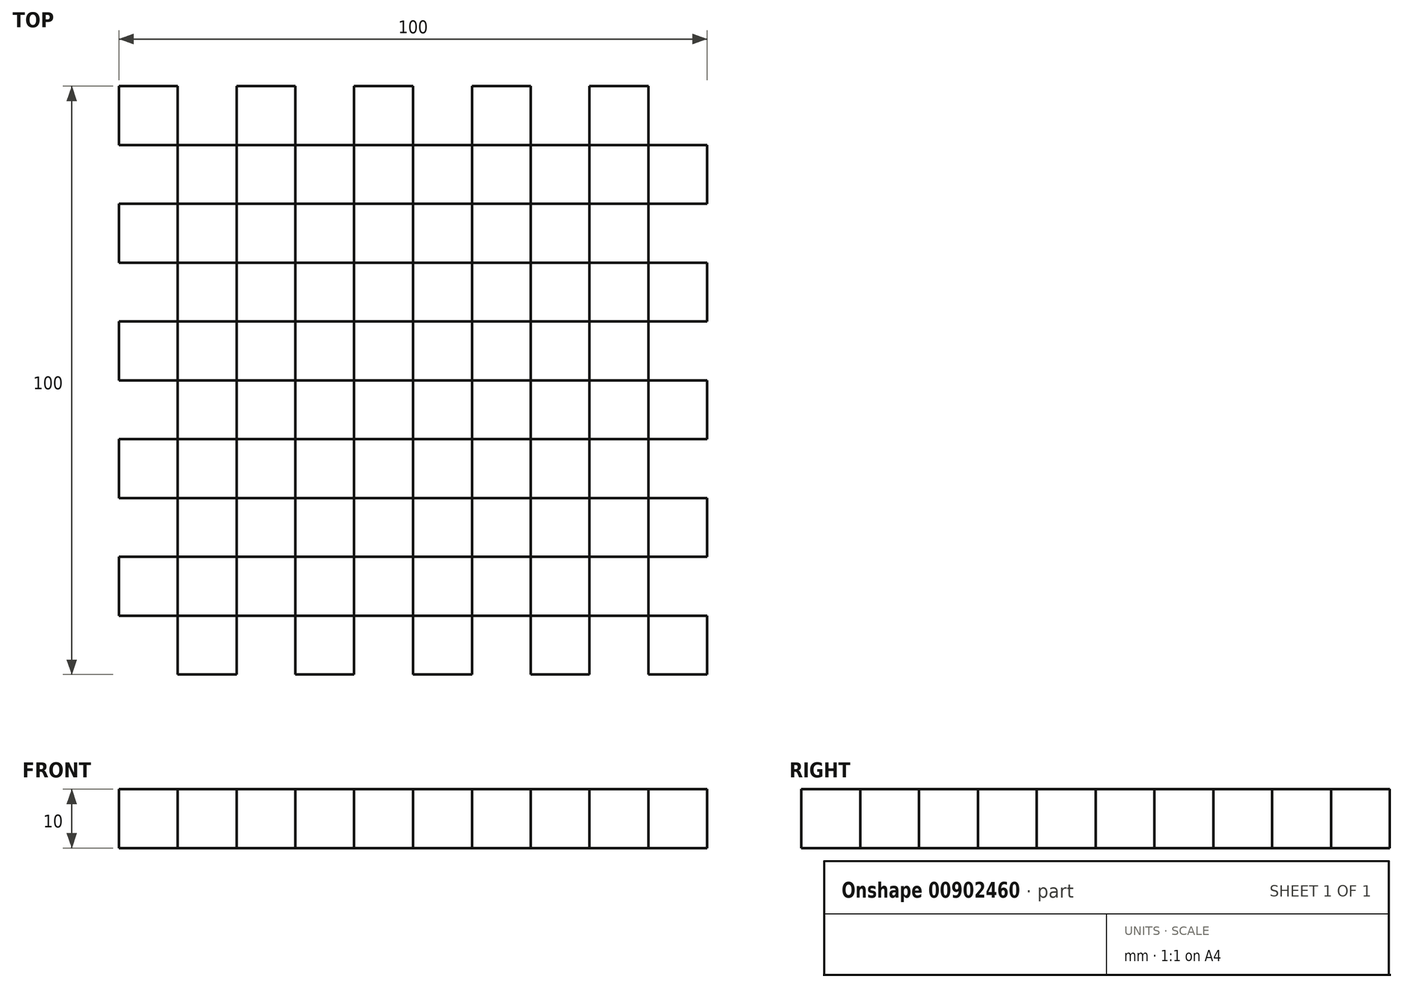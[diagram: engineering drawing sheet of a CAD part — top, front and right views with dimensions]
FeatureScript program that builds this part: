
annotation { "Feature Type Name" : "Feature", "Feature Type Description" : "" }
export const myFeature = defineFeature(function(context is Context, id is Id, definition is map)
    precondition{}
    {
        {
            var Q0;
            Q0=qCreatedBy(makeId("Top.planeOp"),FACE);
            var sketch = newSketch(context, id + "F0", { "sketchPlane" : qUnion([Q0])});
            skLineSegment(sketch, "E0.bottom", {"start": v(-50, 50) * mm, "end": v(50, 50) * mm});
            skLineSegment(sketch, "E0.top", {"start": v(-50, -50) * mm, "end": v(50, -50) * mm});
            skLineSegment(sketch, "E0.left", {"start": v(-50, 50) * mm, "end": v(-50, -50) * mm});
            skLineSegment(sketch, "E0.right", {"start": v(50, 50) * mm, "end": v(50, -50) * mm});
            skLineSegment(sketch, "E1", {"start": v(0, 0) * mm, "end": v(0, 50) * mm, "construction": true});
            skLineSegment(sketch, "E2", {"start": v(0, 0) * mm, "end": v(-50, 0) * mm, "construction": true});
            skLineSegment(sketch, "E3", {"start": v(-50, 40) * mm, "end": v(50, 40) * mm});
            skLineSegment(sketch, "E4", {"start": v(-50, 30) * mm, "end": v(50, 30) * mm});
            skLineSegment(sketch, "E5", {"start": v(-50, 20) * mm, "end": v(50, 20) * mm});
            skLineSegment(sketch, "E6", {"start": v(-50, 10) * mm, "end": v(50, 10) * mm});
            skLineSegment(sketch, "E7", {"start": v(-50, 0) * mm, "end": v(50, 0) * mm});
            skLineSegment(sketch, "E8.MirrorCS", {"start": v(-50, -40) * mm, "end": v(50, -40) * mm});
            skLineSegment(sketch, "E9.MirrorCS", {"start": v(-50, -30) * mm, "end": v(50, -30) * mm});
            skLineSegment(sketch, "E10.MirrorCS", {"start": v(-50, -20) * mm, "end": v(50, -20) * mm});
            skLineSegment(sketch, "E11.MirrorCS", {"start": v(-50, -10) * mm, "end": v(50, -10) * mm});
            skLineSegment(sketch, "E12", {"start": v(-40, 50) * mm, "end": v(-40, -50) * mm});
            skLineSegment(sketch, "E13", {"start": v(-30, 50) * mm, "end": v(-30, -50) * mm});
            skLineSegment(sketch, "E14", {"start": v(-20, 50) * mm, "end": v(-20, -50) * mm});
            skLineSegment(sketch, "E15", {"start": v(-10, 50) * mm, "end": v(-10, -50) * mm});
            skLineSegment(sketch, "E16", {"start": v(0, 50) * mm, "end": v(0, -50) * mm});
            skLineSegment(sketch, "E17.MirrorCS", {"start": v(40, 50) * mm, "end": v(40, -50) * mm});
            skLineSegment(sketch, "E18.MirrorCS", {"start": v(30, 50) * mm, "end": v(30, -50) * mm});
            skLineSegment(sketch, "E19.MirrorCS", {"start": v(20, 50) * mm, "end": v(20, -50) * mm});
            skLineSegment(sketch, "E20.MirrorCS", {"start": v(10, 50) * mm, "end": v(10, -50) * mm});
            skSolve(sketch);
        }
        {
            var Q0;
            {var subQ0=sQuery(id+"F0.wireOp",EDGE,"E0.left");var subQ1=sQuery(id+"F0.wireOp",EDGE,"E0.bottom");var subQ2=makeQuery(id+"F0.imprint","INTERSECT",VERTEX,{"derivedFrom":[subQ1,subQ0]});Q0=makeQuery(id+"F0.imprint","IMPRINT",FACE,{"disambiguationData":[TD([[makeQuery(id+"F0.imprint","IMPRINT",EDGE,{"disambiguationData":[TD([[subQ2,-1.0]])],"derivedFrom":subQ1}),-1.0]])]});}
            var Q1;
            {var subQ0=sQuery(id+"F0.wireOp",EDGE,"E13");var subQ1=sQuery(id+"F0.wireOp",EDGE,"E0.bottom");var subQ2=makeQuery(id+"F0.imprint","INTERSECT",VERTEX,{"derivedFrom":[subQ1,subQ0]});Q1=makeQuery(id+"F0.imprint","IMPRINT",FACE,{"disambiguationData":[TD([[makeQuery(id+"F0.imprint","IMPRINT",EDGE,{"disambiguationData":[TD([[subQ2,-1.0]])],"derivedFrom":subQ1}),-1.0]])]});}
            var Q2;
            {var subQ0=sQuery(id+"F0.wireOp",EDGE,"E15");var subQ1=sQuery(id+"F0.wireOp",EDGE,"E0.bottom");var subQ2=makeQuery(id+"F0.imprint","INTERSECT",VERTEX,{"derivedFrom":[subQ1,subQ0]});Q2=makeQuery(id+"F0.imprint","IMPRINT",FACE,{"disambiguationData":[TD([[makeQuery(id+"F0.imprint","IMPRINT",EDGE,{"disambiguationData":[TD([[subQ2,-1.0]])],"derivedFrom":subQ1}),-1.0]])]});}
            var Q3;
            {var subQ0=sQuery(id+"F0.wireOp",EDGE,"E19.MirrorCS");var subQ1=sQuery(id+"F0.wireOp",EDGE,"E0.bottom");var subQ2=makeQuery(id+"F0.imprint","INTERSECT",VERTEX,{"derivedFrom":[subQ1,subQ0]});Q3=makeQuery(id+"F0.imprint","IMPRINT",FACE,{"disambiguationData":[TD([[makeQuery(id+"F0.imprint","IMPRINT",EDGE,{"disambiguationData":[TD([[subQ2,1.0]])],"derivedFrom":subQ1}),-1.0]])]});}
            var Q4;
            {var subQ0=sQuery(id+"F0.wireOp",EDGE,"E17.MirrorCS");var subQ1=sQuery(id+"F0.wireOp",EDGE,"E0.bottom");var subQ2=makeQuery(id+"F0.imprint","INTERSECT",VERTEX,{"derivedFrom":[subQ1,subQ0]});Q4=makeQuery(id+"F0.imprint","IMPRINT",FACE,{"disambiguationData":[TD([[makeQuery(id+"F0.imprint","IMPRINT",EDGE,{"disambiguationData":[TD([[subQ2,1.0]])],"derivedFrom":subQ1}),-1.0]])]});}
            var Q5;
            {var subQ0=sQuery(id+"F0.wireOp",EDGE,"E3");var subQ1=sQuery(id+"F0.wireOp",EDGE,"E0.right");var subQ2=makeQuery(id+"F0.imprint","INTERSECT",VERTEX,{"derivedFrom":[subQ1,subQ0]});Q5=makeQuery(id+"F0.imprint","IMPRINT",FACE,{"disambiguationData":[TD([[makeQuery(id+"F0.imprint","IMPRINT",EDGE,{"disambiguationData":[TD([[subQ2,-1.0]])],"derivedFrom":subQ1}),-1.0]])]});}
            var Q6;
            {var subQ0=sQuery(id+"F0.wireOp",EDGE,"E19.MirrorCS");var subQ1=sQuery(id+"F0.wireOp",EDGE,"E3");var subQ2=makeQuery(id+"F0.imprint","INTERSECT",VERTEX,{"derivedFrom":[subQ1,subQ0]});Q6=makeQuery(id+"F0.imprint","IMPRINT",FACE,{"disambiguationData":[TD([[makeQuery(id+"F0.imprint","IMPRINT",EDGE,{"disambiguationData":[TD([[subQ2,-1.0]])],"derivedFrom":subQ1}),-1.0]])]});}
            var Q7;
            {var subQ0=sQuery(id+"F0.wireOp",EDGE,"E16");var subQ1=sQuery(id+"F0.wireOp",EDGE,"E3");var subQ2=makeQuery(id+"F0.imprint","INTERSECT",VERTEX,{"derivedFrom":[subQ1,subQ0]});Q7=makeQuery(id+"F0.imprint","IMPRINT",FACE,{"disambiguationData":[TD([[makeQuery(id+"F0.imprint","IMPRINT",EDGE,{"disambiguationData":[TD([[subQ2,-1.0]])],"derivedFrom":subQ1}),-1.0]])]});}
            var Q8;
            {var subQ0=sQuery(id+"F0.wireOp",EDGE,"E14");var subQ1=sQuery(id+"F0.wireOp",EDGE,"E3");var subQ2=makeQuery(id+"F0.imprint","INTERSECT",VERTEX,{"derivedFrom":[subQ1,subQ0]});Q8=makeQuery(id+"F0.imprint","IMPRINT",FACE,{"disambiguationData":[TD([[makeQuery(id+"F0.imprint","IMPRINT",EDGE,{"disambiguationData":[TD([[subQ2,-1.0]])],"derivedFrom":subQ1}),-1.0]])]});}
            var Q9;
            {var subQ0=sQuery(id+"F0.wireOp",EDGE,"E12");var subQ1=sQuery(id+"F0.wireOp",EDGE,"E3");var subQ2=makeQuery(id+"F0.imprint","INTERSECT",VERTEX,{"derivedFrom":[subQ1,subQ0]});Q9=makeQuery(id+"F0.imprint","IMPRINT",FACE,{"disambiguationData":[TD([[makeQuery(id+"F0.imprint","IMPRINT",EDGE,{"disambiguationData":[TD([[subQ2,-1.0]])],"derivedFrom":subQ1}),-1.0]])]});}
            var Q10;
            {var subQ0=sQuery(id+"F0.wireOp",EDGE,"E4");var subQ1=sQuery(id+"F0.wireOp",EDGE,"E0.left");var subQ2=makeQuery(id+"F0.imprint","INTERSECT",VERTEX,{"derivedFrom":[subQ1,subQ0]});Q10=makeQuery(id+"F0.imprint","IMPRINT",FACE,{"disambiguationData":[TD([[makeQuery(id+"F0.imprint","IMPRINT",EDGE,{"disambiguationData":[TD([[subQ2,-1.0]])],"derivedFrom":subQ1}),1.0]])]});}
            var Q11;
            {var subQ0=sQuery(id+"F0.wireOp",EDGE,"E13");var subQ1=sQuery(id+"F0.wireOp",EDGE,"E4");var subQ2=makeQuery(id+"F0.imprint","INTERSECT",VERTEX,{"derivedFrom":[subQ1,subQ0]});Q11=makeQuery(id+"F0.imprint","IMPRINT",FACE,{"disambiguationData":[TD([[makeQuery(id+"F0.imprint","IMPRINT",EDGE,{"disambiguationData":[TD([[subQ2,-1.0]])],"derivedFrom":subQ1}),-1.0]])]});}
            var Q12;
            {var subQ0=sQuery(id+"F0.wireOp",EDGE,"E15");var subQ1=sQuery(id+"F0.wireOp",EDGE,"E4");var subQ2=makeQuery(id+"F0.imprint","INTERSECT",VERTEX,{"derivedFrom":[subQ1,subQ0]});Q12=makeQuery(id+"F0.imprint","IMPRINT",FACE,{"disambiguationData":[TD([[makeQuery(id+"F0.imprint","IMPRINT",EDGE,{"disambiguationData":[TD([[subQ2,-1.0]])],"derivedFrom":subQ1}),-1.0]])]});}
            var Q13;
            {var subQ0=sQuery(id+"F0.wireOp",EDGE,"E20.MirrorCS");var subQ1=sQuery(id+"F0.wireOp",EDGE,"E4");var subQ2=makeQuery(id+"F0.imprint","INTERSECT",VERTEX,{"derivedFrom":[subQ1,subQ0]});Q13=makeQuery(id+"F0.imprint","IMPRINT",FACE,{"disambiguationData":[TD([[makeQuery(id+"F0.imprint","IMPRINT",EDGE,{"disambiguationData":[TD([[subQ2,-1.0]])],"derivedFrom":subQ1}),-1.0]])]});}
            var Q14;
            {var subQ0=sQuery(id+"F0.wireOp",EDGE,"E18.MirrorCS");var subQ1=sQuery(id+"F0.wireOp",EDGE,"E4");var subQ2=makeQuery(id+"F0.imprint","INTERSECT",VERTEX,{"derivedFrom":[subQ1,subQ0]});Q14=makeQuery(id+"F0.imprint","IMPRINT",FACE,{"disambiguationData":[TD([[makeQuery(id+"F0.imprint","IMPRINT",EDGE,{"disambiguationData":[TD([[subQ2,-1.0]])],"derivedFrom":subQ1}),-1.0]])]});}
            var Q15;
            {var subQ0=sQuery(id+"F0.wireOp",EDGE,"E5");var subQ1=sQuery(id+"F0.wireOp",EDGE,"E0.right");var subQ2=makeQuery(id+"F0.imprint","INTERSECT",VERTEX,{"derivedFrom":[subQ1,subQ0]});Q15=makeQuery(id+"F0.imprint","IMPRINT",FACE,{"disambiguationData":[TD([[makeQuery(id+"F0.imprint","IMPRINT",EDGE,{"disambiguationData":[TD([[subQ2,-1.0]])],"derivedFrom":subQ1}),-1.0]])]});}
            var Q16;
            {var subQ0=sQuery(id+"F0.wireOp",EDGE,"E19.MirrorCS");var subQ1=sQuery(id+"F0.wireOp",EDGE,"E5");var subQ2=makeQuery(id+"F0.imprint","INTERSECT",VERTEX,{"derivedFrom":[subQ1,subQ0]});Q16=makeQuery(id+"F0.imprint","IMPRINT",FACE,{"disambiguationData":[TD([[makeQuery(id+"F0.imprint","IMPRINT",EDGE,{"disambiguationData":[TD([[subQ2,-1.0]])],"derivedFrom":subQ1}),-1.0]])]});}
            var Q17;
            {var subQ0=sQuery(id+"F0.wireOp",EDGE,"E16");var subQ1=sQuery(id+"F0.wireOp",EDGE,"E5");var subQ2=makeQuery(id+"F0.imprint","INTERSECT",VERTEX,{"derivedFrom":[subQ1,subQ0]});Q17=makeQuery(id+"F0.imprint","IMPRINT",FACE,{"disambiguationData":[TD([[makeQuery(id+"F0.imprint","IMPRINT",EDGE,{"disambiguationData":[TD([[subQ2,-1.0]])],"derivedFrom":subQ1}),-1.0]])]});}
            var Q18;
            {var subQ0=sQuery(id+"F0.wireOp",EDGE,"E14");var subQ1=sQuery(id+"F0.wireOp",EDGE,"E5");var subQ2=makeQuery(id+"F0.imprint","INTERSECT",VERTEX,{"derivedFrom":[subQ1,subQ0]});Q18=makeQuery(id+"F0.imprint","IMPRINT",FACE,{"disambiguationData":[TD([[makeQuery(id+"F0.imprint","IMPRINT",EDGE,{"disambiguationData":[TD([[subQ2,-1.0]])],"derivedFrom":subQ1}),-1.0]])]});}
            var Q19;
            {var subQ0=sQuery(id+"F0.wireOp",EDGE,"E12");var subQ1=sQuery(id+"F0.wireOp",EDGE,"E5");var subQ2=makeQuery(id+"F0.imprint","INTERSECT",VERTEX,{"derivedFrom":[subQ1,subQ0]});Q19=makeQuery(id+"F0.imprint","IMPRINT",FACE,{"disambiguationData":[TD([[makeQuery(id+"F0.imprint","IMPRINT",EDGE,{"disambiguationData":[TD([[subQ2,-1.0]])],"derivedFrom":subQ1}),-1.0]])]});}
            var Q20;
            {var subQ0=sQuery(id+"F0.wireOp",EDGE,"E6");var subQ1=sQuery(id+"F0.wireOp",EDGE,"E0.left");var subQ2=makeQuery(id+"F0.imprint","INTERSECT",VERTEX,{"derivedFrom":[subQ1,subQ0]});Q20=makeQuery(id+"F0.imprint","IMPRINT",FACE,{"disambiguationData":[TD([[makeQuery(id+"F0.imprint","IMPRINT",EDGE,{"disambiguationData":[TD([[subQ2,-1.0]])],"derivedFrom":subQ1}),1.0]])]});}
            var Q21;
            {var subQ0=sQuery(id+"F0.wireOp",EDGE,"E13");var subQ1=sQuery(id+"F0.wireOp",EDGE,"E6");var subQ2=makeQuery(id+"F0.imprint","INTERSECT",VERTEX,{"derivedFrom":[subQ1,subQ0]});Q21=makeQuery(id+"F0.imprint","IMPRINT",FACE,{"disambiguationData":[TD([[makeQuery(id+"F0.imprint","IMPRINT",EDGE,{"disambiguationData":[TD([[subQ2,-1.0]])],"derivedFrom":subQ1}),-1.0]])]});}
            var Q22;
            {var subQ0=sQuery(id+"F0.wireOp",EDGE,"E15");var subQ1=sQuery(id+"F0.wireOp",EDGE,"E6");var subQ2=makeQuery(id+"F0.imprint","INTERSECT",VERTEX,{"derivedFrom":[subQ1,subQ0]});Q22=makeQuery(id+"F0.imprint","IMPRINT",FACE,{"disambiguationData":[TD([[makeQuery(id+"F0.imprint","IMPRINT",EDGE,{"disambiguationData":[TD([[subQ2,-1.0]])],"derivedFrom":subQ1}),-1.0]])]});}
            var Q23;
            {var subQ0=sQuery(id+"F0.wireOp",EDGE,"E20.MirrorCS");var subQ1=sQuery(id+"F0.wireOp",EDGE,"E6");var subQ2=makeQuery(id+"F0.imprint","INTERSECT",VERTEX,{"derivedFrom":[subQ1,subQ0]});Q23=makeQuery(id+"F0.imprint","IMPRINT",FACE,{"disambiguationData":[TD([[makeQuery(id+"F0.imprint","IMPRINT",EDGE,{"disambiguationData":[TD([[subQ2,-1.0]])],"derivedFrom":subQ1}),-1.0]])]});}
            var Q24;
            {var subQ0=sQuery(id+"F0.wireOp",EDGE,"E18.MirrorCS");var subQ1=sQuery(id+"F0.wireOp",EDGE,"E6");var subQ2=makeQuery(id+"F0.imprint","INTERSECT",VERTEX,{"derivedFrom":[subQ1,subQ0]});Q24=makeQuery(id+"F0.imprint","IMPRINT",FACE,{"disambiguationData":[TD([[makeQuery(id+"F0.imprint","IMPRINT",EDGE,{"disambiguationData":[TD([[subQ2,-1.0]])],"derivedFrom":subQ1}),-1.0]])]});}
            var Q25;
            {var subQ0=sQuery(id+"F0.wireOp",EDGE,"E7");var subQ1=sQuery(id+"F0.wireOp",EDGE,"E0.right");var subQ2=makeQuery(id+"F0.imprint","INTERSECT",VERTEX,{"derivedFrom":[subQ1,subQ0]});Q25=makeQuery(id+"F0.imprint","IMPRINT",FACE,{"disambiguationData":[TD([[makeQuery(id+"F0.imprint","IMPRINT",EDGE,{"disambiguationData":[TD([[subQ2,-1.0]])],"derivedFrom":subQ1}),-1.0]])]});}
            var Q26;
            {var subQ0=sQuery(id+"F0.wireOp",EDGE,"E19.MirrorCS");var subQ1=sQuery(id+"F0.wireOp",EDGE,"E7");var subQ2=makeQuery(id+"F0.imprint","INTERSECT",VERTEX,{"derivedFrom":[subQ1,subQ0]});Q26=makeQuery(id+"F0.imprint","IMPRINT",FACE,{"disambiguationData":[TD([[makeQuery(id+"F0.imprint","IMPRINT",EDGE,{"disambiguationData":[TD([[subQ2,-1.0]])],"derivedFrom":subQ1}),-1.0]])]});}
            var Q27;
            {var subQ0=sQuery(id+"F0.wireOp",EDGE,"E16");var subQ1=sQuery(id+"F0.wireOp",EDGE,"E7");var subQ2=makeQuery(id+"F0.imprint","INTERSECT",VERTEX,{"derivedFrom":[subQ1,subQ0]});Q27=makeQuery(id+"F0.imprint","IMPRINT",FACE,{"disambiguationData":[TD([[makeQuery(id+"F0.imprint","IMPRINT",EDGE,{"disambiguationData":[TD([[subQ2,-1.0]])],"derivedFrom":subQ1}),-1.0]])]});}
            var Q28;
            {var subQ0=sQuery(id+"F0.wireOp",EDGE,"E14");var subQ1=sQuery(id+"F0.wireOp",EDGE,"E7");var subQ2=makeQuery(id+"F0.imprint","INTERSECT",VERTEX,{"derivedFrom":[subQ1,subQ0]});Q28=makeQuery(id+"F0.imprint","IMPRINT",FACE,{"disambiguationData":[TD([[makeQuery(id+"F0.imprint","IMPRINT",EDGE,{"disambiguationData":[TD([[subQ2,-1.0]])],"derivedFrom":subQ1}),-1.0]])]});}
            var Q29;
            {var subQ0=sQuery(id+"F0.wireOp",EDGE,"E12");var subQ1=sQuery(id+"F0.wireOp",EDGE,"E7");var subQ2=makeQuery(id+"F0.imprint","INTERSECT",VERTEX,{"derivedFrom":[subQ1,subQ0]});Q29=makeQuery(id+"F0.imprint","IMPRINT",FACE,{"disambiguationData":[TD([[makeQuery(id+"F0.imprint","IMPRINT",EDGE,{"disambiguationData":[TD([[subQ2,-1.0]])],"derivedFrom":subQ1}),-1.0]])]});}
            var Q30;
            {var subQ0=sQuery(id+"F0.wireOp",EDGE,"E10.MirrorCS");var subQ1=sQuery(id+"F0.wireOp",EDGE,"E0.left");var subQ2=makeQuery(id+"F0.imprint","INTERSECT",VERTEX,{"derivedFrom":[subQ1,subQ0]});Q30=makeQuery(id+"F0.imprint","IMPRINT",FACE,{"disambiguationData":[TD([[makeQuery(id+"F0.imprint","IMPRINT",EDGE,{"disambiguationData":[TD([[subQ2,1.0]])],"derivedFrom":subQ1}),1.0]])]});}
            var Q31;
            {var subQ0=sQuery(id+"F0.wireOp",EDGE,"E13");var subQ1=sQuery(id+"F0.wireOp",EDGE,"E10.MirrorCS");var subQ2=makeQuery(id+"F0.imprint","INTERSECT",VERTEX,{"derivedFrom":[subQ1,subQ0]});Q31=makeQuery(id+"F0.imprint","IMPRINT",FACE,{"disambiguationData":[TD([[makeQuery(id+"F0.imprint","IMPRINT",EDGE,{"disambiguationData":[TD([[subQ2,-1.0]])],"derivedFrom":subQ1}),1.0]])]});}
            var Q32;
            {var subQ0=sQuery(id+"F0.wireOp",EDGE,"E15");var subQ1=sQuery(id+"F0.wireOp",EDGE,"E10.MirrorCS");var subQ2=makeQuery(id+"F0.imprint","INTERSECT",VERTEX,{"derivedFrom":[subQ1,subQ0]});Q32=makeQuery(id+"F0.imprint","IMPRINT",FACE,{"disambiguationData":[TD([[makeQuery(id+"F0.imprint","IMPRINT",EDGE,{"disambiguationData":[TD([[subQ2,-1.0]])],"derivedFrom":subQ1}),1.0]])]});}
            var Q33;
            {var subQ0=sQuery(id+"F0.wireOp",EDGE,"E20.MirrorCS");var subQ1=sQuery(id+"F0.wireOp",EDGE,"E10.MirrorCS");var subQ2=makeQuery(id+"F0.imprint","INTERSECT",VERTEX,{"derivedFrom":[subQ1,subQ0]});Q33=makeQuery(id+"F0.imprint","IMPRINT",FACE,{"disambiguationData":[TD([[makeQuery(id+"F0.imprint","IMPRINT",EDGE,{"disambiguationData":[TD([[subQ2,-1.0]])],"derivedFrom":subQ1}),1.0]])]});}
            var Q34;
            {var subQ0=sQuery(id+"F0.wireOp",EDGE,"E18.MirrorCS");var subQ1=sQuery(id+"F0.wireOp",EDGE,"E10.MirrorCS");var subQ2=makeQuery(id+"F0.imprint","INTERSECT",VERTEX,{"derivedFrom":[subQ1,subQ0]});Q34=makeQuery(id+"F0.imprint","IMPRINT",FACE,{"disambiguationData":[TD([[makeQuery(id+"F0.imprint","IMPRINT",EDGE,{"disambiguationData":[TD([[subQ2,-1.0]])],"derivedFrom":subQ1}),1.0]])]});}
            var Q35;
            {var subQ0=sQuery(id+"F0.wireOp",EDGE,"E9.MirrorCS");var subQ1=sQuery(id+"F0.wireOp",EDGE,"E0.right");var subQ2=makeQuery(id+"F0.imprint","INTERSECT",VERTEX,{"derivedFrom":[subQ1,subQ0]});Q35=makeQuery(id+"F0.imprint","IMPRINT",FACE,{"disambiguationData":[TD([[makeQuery(id+"F0.imprint","IMPRINT",EDGE,{"disambiguationData":[TD([[subQ2,1.0]])],"derivedFrom":subQ1}),-1.0]])]});}
            var Q36;
            {var subQ0=sQuery(id+"F0.wireOp",EDGE,"E19.MirrorCS");var subQ1=sQuery(id+"F0.wireOp",EDGE,"E9.MirrorCS");var subQ2=makeQuery(id+"F0.imprint","INTERSECT",VERTEX,{"derivedFrom":[subQ1,subQ0]});Q36=makeQuery(id+"F0.imprint","IMPRINT",FACE,{"disambiguationData":[TD([[makeQuery(id+"F0.imprint","IMPRINT",EDGE,{"disambiguationData":[TD([[subQ2,-1.0]])],"derivedFrom":subQ1}),1.0]])]});}
            var Q37;
            {var subQ0=sQuery(id+"F0.wireOp",EDGE,"E16");var subQ1=sQuery(id+"F0.wireOp",EDGE,"E9.MirrorCS");var subQ2=makeQuery(id+"F0.imprint","INTERSECT",VERTEX,{"derivedFrom":[subQ1,subQ0]});Q37=makeQuery(id+"F0.imprint","IMPRINT",FACE,{"disambiguationData":[TD([[makeQuery(id+"F0.imprint","IMPRINT",EDGE,{"disambiguationData":[TD([[subQ2,-1.0]])],"derivedFrom":subQ1}),1.0]])]});}
            var Q38;
            {var subQ0=sQuery(id+"F0.wireOp",EDGE,"E14");var subQ1=sQuery(id+"F0.wireOp",EDGE,"E9.MirrorCS");var subQ2=makeQuery(id+"F0.imprint","INTERSECT",VERTEX,{"derivedFrom":[subQ1,subQ0]});Q38=makeQuery(id+"F0.imprint","IMPRINT",FACE,{"disambiguationData":[TD([[makeQuery(id+"F0.imprint","IMPRINT",EDGE,{"disambiguationData":[TD([[subQ2,-1.0]])],"derivedFrom":subQ1}),1.0]])]});}
            var Q39;
            {var subQ0=sQuery(id+"F0.wireOp",EDGE,"E12");var subQ1=sQuery(id+"F0.wireOp",EDGE,"E9.MirrorCS");var subQ2=makeQuery(id+"F0.imprint","INTERSECT",VERTEX,{"derivedFrom":[subQ1,subQ0]});Q39=makeQuery(id+"F0.imprint","IMPRINT",FACE,{"disambiguationData":[TD([[makeQuery(id+"F0.imprint","IMPRINT",EDGE,{"disambiguationData":[TD([[subQ2,-1.0]])],"derivedFrom":subQ1}),1.0]])]});}
            var Q40;
            {var subQ0=sQuery(id+"F0.wireOp",EDGE,"E8.MirrorCS");var subQ1=sQuery(id+"F0.wireOp",EDGE,"E0.left");var subQ2=makeQuery(id+"F0.imprint","INTERSECT",VERTEX,{"derivedFrom":[subQ1,subQ0]});Q40=makeQuery(id+"F0.imprint","IMPRINT",FACE,{"disambiguationData":[TD([[makeQuery(id+"F0.imprint","IMPRINT",EDGE,{"disambiguationData":[TD([[subQ2,1.0]])],"derivedFrom":subQ1}),1.0]])]});}
            var Q41;
            {var subQ0=sQuery(id+"F0.wireOp",EDGE,"E13");var subQ1=sQuery(id+"F0.wireOp",EDGE,"E8.MirrorCS");var subQ2=makeQuery(id+"F0.imprint","INTERSECT",VERTEX,{"derivedFrom":[subQ1,subQ0]});Q41=makeQuery(id+"F0.imprint","IMPRINT",FACE,{"disambiguationData":[TD([[makeQuery(id+"F0.imprint","IMPRINT",EDGE,{"disambiguationData":[TD([[subQ2,-1.0]])],"derivedFrom":subQ1}),1.0]])]});}
            var Q42;
            {var subQ0=sQuery(id+"F0.wireOp",EDGE,"E15");var subQ1=sQuery(id+"F0.wireOp",EDGE,"E8.MirrorCS");var subQ2=makeQuery(id+"F0.imprint","INTERSECT",VERTEX,{"derivedFrom":[subQ1,subQ0]});Q42=makeQuery(id+"F0.imprint","IMPRINT",FACE,{"disambiguationData":[TD([[makeQuery(id+"F0.imprint","IMPRINT",EDGE,{"disambiguationData":[TD([[subQ2,-1.0]])],"derivedFrom":subQ1}),1.0]])]});}
            var Q43;
            {var subQ0=sQuery(id+"F0.wireOp",EDGE,"E20.MirrorCS");var subQ1=sQuery(id+"F0.wireOp",EDGE,"E8.MirrorCS");var subQ2=makeQuery(id+"F0.imprint","INTERSECT",VERTEX,{"derivedFrom":[subQ1,subQ0]});Q43=makeQuery(id+"F0.imprint","IMPRINT",FACE,{"disambiguationData":[TD([[makeQuery(id+"F0.imprint","IMPRINT",EDGE,{"disambiguationData":[TD([[subQ2,-1.0]])],"derivedFrom":subQ1}),1.0]])]});}
            var Q44;
            {var subQ0=sQuery(id+"F0.wireOp",EDGE,"E18.MirrorCS");var subQ1=sQuery(id+"F0.wireOp",EDGE,"E8.MirrorCS");var subQ2=makeQuery(id+"F0.imprint","INTERSECT",VERTEX,{"derivedFrom":[subQ1,subQ0]});Q44=makeQuery(id+"F0.imprint","IMPRINT",FACE,{"disambiguationData":[TD([[makeQuery(id+"F0.imprint","IMPRINT",EDGE,{"disambiguationData":[TD([[subQ2,-1.0]])],"derivedFrom":subQ1}),1.0]])]});}
            var Q45;
            {var subQ0=sQuery(id+"F0.wireOp",EDGE,"E0.top");var subQ1=sQuery(id+"F0.wireOp",EDGE,"E0.right");var subQ2=makeQuery(id+"F0.imprint","INTERSECT",VERTEX,{"derivedFrom":[subQ1,subQ0]});Q45=makeQuery(id+"F0.imprint","IMPRINT",FACE,{"disambiguationData":[TD([[makeQuery(id+"F0.imprint","IMPRINT",EDGE,{"disambiguationData":[TD([[subQ2,1.0]])],"derivedFrom":subQ1}),-1.0]])]});}
            var Q46;
            {var subQ0=sQuery(id+"F0.wireOp",EDGE,"E18.MirrorCS");var subQ1=sQuery(id+"F0.wireOp",EDGE,"E0.top");var subQ2=makeQuery(id+"F0.imprint","INTERSECT",VERTEX,{"derivedFrom":[subQ1,subQ0]});Q46=makeQuery(id+"F0.imprint","IMPRINT",FACE,{"disambiguationData":[TD([[makeQuery(id+"F0.imprint","IMPRINT",EDGE,{"disambiguationData":[TD([[subQ2,1.0]])],"derivedFrom":subQ1}),1.0]])]});}
            var Q47;
            {var subQ0=sQuery(id+"F0.wireOp",EDGE,"E16");var subQ1=sQuery(id+"F0.wireOp",EDGE,"E0.top");var subQ2=makeQuery(id+"F0.imprint","INTERSECT",VERTEX,{"derivedFrom":[subQ1,subQ0]});Q47=makeQuery(id+"F0.imprint","IMPRINT",FACE,{"disambiguationData":[TD([[makeQuery(id+"F0.imprint","IMPRINT",EDGE,{"disambiguationData":[TD([[subQ2,-1.0]])],"derivedFrom":subQ1}),1.0]])]});}
            var Q48;
            {var subQ0=sQuery(id+"F0.wireOp",EDGE,"E14");var subQ1=sQuery(id+"F0.wireOp",EDGE,"E0.top");var subQ2=makeQuery(id+"F0.imprint","INTERSECT",VERTEX,{"derivedFrom":[subQ1,subQ0]});Q48=makeQuery(id+"F0.imprint","IMPRINT",FACE,{"disambiguationData":[TD([[makeQuery(id+"F0.imprint","IMPRINT",EDGE,{"disambiguationData":[TD([[subQ2,-1.0]])],"derivedFrom":subQ1}),1.0]])]});}
            var Q49;
            {var subQ0=sQuery(id+"F0.wireOp",EDGE,"E12");var subQ1=sQuery(id+"F0.wireOp",EDGE,"E0.top");var subQ2=makeQuery(id+"F0.imprint","INTERSECT",VERTEX,{"derivedFrom":[subQ1,subQ0]});Q49=makeQuery(id+"F0.imprint","IMPRINT",FACE,{"disambiguationData":[TD([[makeQuery(id+"F0.imprint","IMPRINT",EDGE,{"disambiguationData":[TD([[subQ2,-1.0]])],"derivedFrom":subQ1}),1.0]])]});}
            extrude(context, id + "F1", {"entities" : qUnion([Q0, Q1, Q2, Q3, Q4, Q5, Q6, Q7, Q8, Q9, Q10, Q11, Q12, Q13, Q14, Q15, Q16, Q17, Q18, Q19, Q20, Q21, Q22, Q23, Q24, Q25, Q26, Q27, Q28, Q29, Q30, Q31, Q32, Q33, Q34, Q35, Q36, Q37, Q38, Q39, Q40, Q41, Q42, Q43, Q44, Q45, Q46, Q47, Q48, Q49]), "depth" : 10 * mm, "offsetDistance" : 25 * mm});
        }
    });
